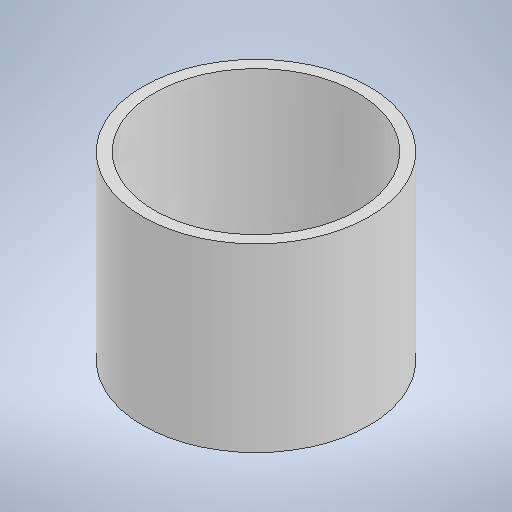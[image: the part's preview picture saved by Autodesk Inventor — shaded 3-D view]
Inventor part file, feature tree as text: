
AUTODESK INVENTOR PART (.ipt)
format: ipt  version: 2025 (Build 290162000, 162)  size: 209,408 bytes
history: native  units: mm
features: sketch x5, extrude x3, other x1
ambient origin geometry x8: Origin, YZ Plane, XZ Plane, XY Plane, X Axis, Y Axis, Z Axis, Center Point
bodies: Body1 (feature_tree)
feature tree (9):
  other  "Bryła1"
  extrude  "Wyciągnięcie proste1"  Depth=100.0mm
  extrude  "Wyciągnięcie proste2"  Depth=80.0mm TaperAngle=0.0deg
  sketch  "Szkic3"
  extrude  "Wyciągnięcie proste3"  Depth=90.0mm
  sketch  "Szkic9"
  sketch  "Szkic1"
  sketch  "Szkic2"
  sketch  "Szkic4"
